# Revit family: Faucet-Kitchen-KOHLER-Parallel-K-32456T
name_source: partatom
category: Plumbing Fixtures
units: mm (PartAtom-declared; Revit-internal decimal feet)

## family parameters
Cut with Voids When Loaded = No
Host = Face
OmniClass Number = 23.31.11.00
OmniClass Title = Faucets
Part Type = Normal
Room Calculation Point = No
Round Connector Dimension = Use Diameter
Shared = No

## types (3) — shared parameters
ADA Compliant = No
Assembly Code = D2010
CW Connection = Yes
Cold Water Inlet = Cold Water Inlet
Date Modified = 08/06/2024
Default Elevation = 36"
Description = PARALLEL PULL OUT KITCHEN FAUCET
Drain Included = No
Flow Rate = 2 GPM
HW Connection = Yes
Height = 12 5/16"
Hot Water Inlet = Hot Water Inlet
Length = 7 11/16"
Manufacturer = Kohler Co.
Master Format 2014 = 22 41 39
Master Format 2014 Name = Residential Faucets, Supplies, and Trim
Material = Premium Metal Construction
Pressure = 60.00 psi
Product Name = Parallel
Spout Reach = 7 11/16"
URL = http://www.kohler.com.cn
Vent Connection = No
Waste Connection = No
Waste Water Outlet = Waste Water Outlet
WaterSense Certified = No
Width = 2 3/8"

## per-type parameters (varying)
| type | Finish | Model | Secondary Finish | Type |
| CP-Polished Chrome | Kohler-Metal-CP-Polished_Chrome | K-32456T-7-CP | Kohler-Metal-G-Brushed_Chrome | 2 |
| BL-Matte Black | Kohler-Metal-BL-Matte_Black | K-32456T-7-BL | Kohler-Metal-SN-Vibrant_Polished_Nickel | 1 |
| VS-Vibrant Stainless | Kohler-Metal-VS-Vibrant_Stainless | K-32456T-7-VS | Kohler-Metal-VS-Vibrant_Stainless | 3 |

## geometry (parser evidence)
native form markers: Sweep x4
no freeform markers — native parametric forms only
